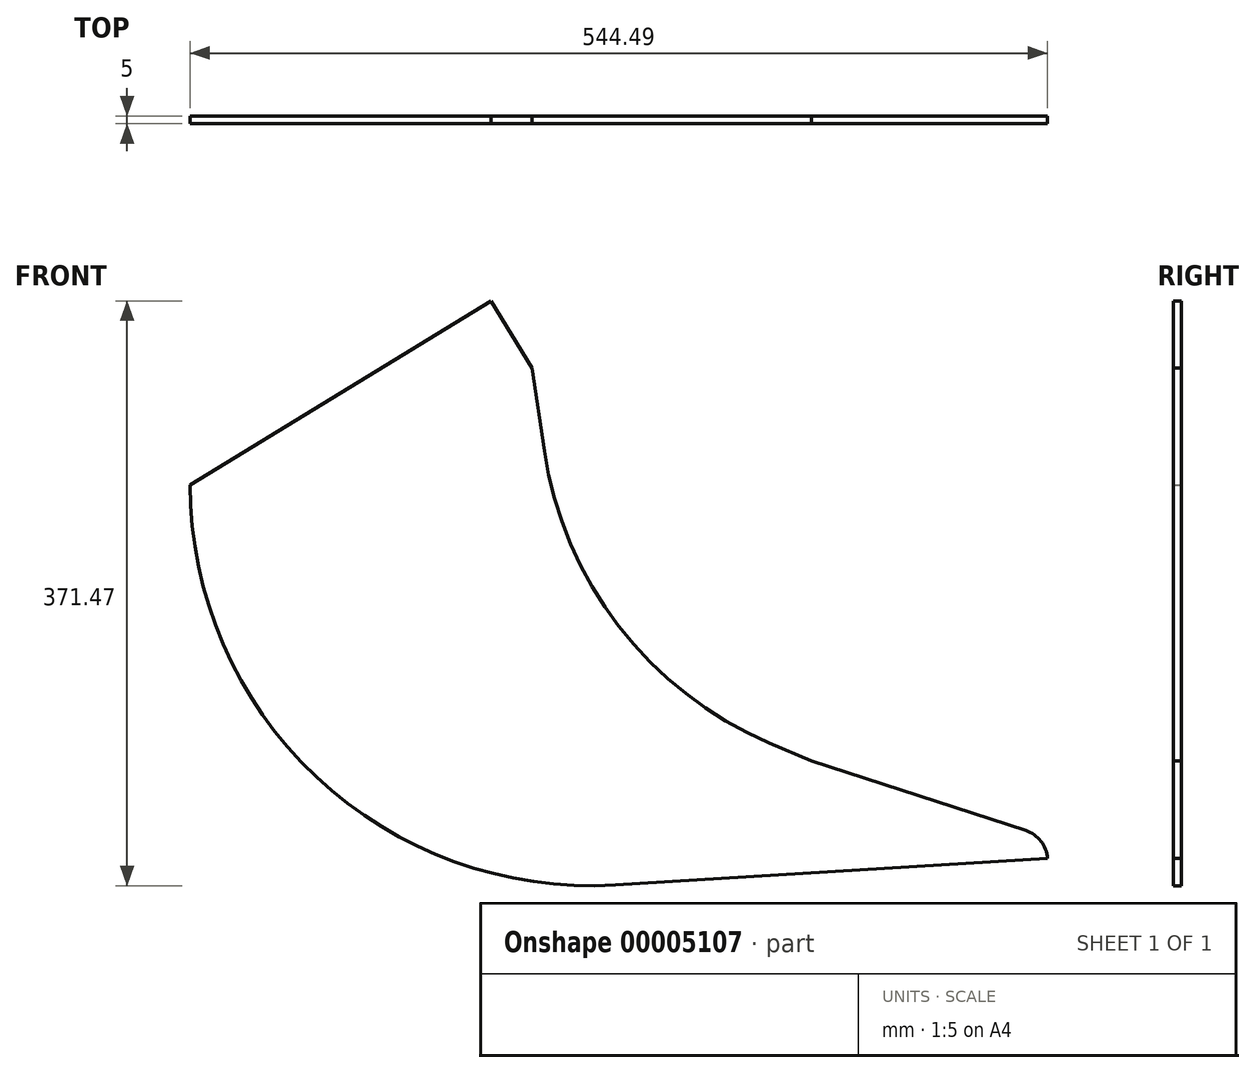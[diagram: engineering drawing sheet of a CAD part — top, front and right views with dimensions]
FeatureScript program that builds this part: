
annotation { "Feature Type Name" : "Feature", "Feature Type Description" : "" }
export const myFeature = defineFeature(function(context is Context, id is Id, definition is map)
    precondition{}
    {
        {
            var Q0;
            Q0=qCreatedBy(makeId("Front.planeOp"),FACE);
            var sketch = newSketch(context, id + "F0", { "sketchPlane" : qUnion([Q0])});
            skPoint(sketch, "E0.visualSharp", {"position": v(-263.52, -268.43) * mm});
            skArc(sketch, "E1", {"start": v(-326.76, 0) * mm, "mid": v(-246.64, -185.33) * mm, "end": v(-56.76, -253.99) * mm});
            skLineSegment(sketch, "E2", {"start": v(-56.76, -253.99) * mm, "end": v(217.73, -237.24) * mm});
            skLineSegment(sketch, "E3", {"start": v(217.73, -237.24) * mm, "end": v(217.73, -237.24) * mm});
            skLineSegment(sketch, "E4", {"start": v(-326.76, 0) * mm, "end": v(-135.75, 117.01) * mm});
            skLineSegment(sketch, "E5", {"start": v(-135.75, 117.01) * mm, "end": v(-109.64, 74.38) * mm});
            skLineSegment(sketch, "E6", {"start": v(-110.08, 75.56) * mm, "end": v(-109.64, 74.38) * mm});
            skLineSegment(sketch, "E7", {"start": v(67.92, -175.3) * mm, "end": v(203.94, -219.44) * mm});
            skPoint(sketch, "E8.visualSharp", {"position": v(216.9, -223.64) * mm});
            skArc(sketch, "E8.filletArc", {"start": v(217.73, -237.24) * mm, "mid": v(213.58, -226.21) * mm, "end": v(203.94, -219.44) * mm});
            skLineSegment(sketch, "E9", {"start": v(-109.64, 74.38) * mm, "end": v(-101.84, 21.7) * mm});
            skLineSegment(sketch, "E10", {"start": v(40.95, -163.72) * mm, "end": v(67.92, -175.3) * mm});
            skPoint(sketch, "E11.visualSharp", {"position": v(-82.22, -110.88) * mm});
            skArc(sketch, "E11.filletArc", {"start": v(-101.84, 21.7) * mm, "mid": v(-54.58, -89.6) * mm, "end": v(40.95, -163.72) * mm});
            skSolve(sketch);
        }
        {
            var Q0;
            Q0=makeQuery(id+"F0.imprint","IMPRINT",FACE,{"disambiguationData":[TD([[makeQuery(id+"F0.imprint","IMPRINT",EDGE,{"derivedFrom":sQuery(id+"F0.wireOp",EDGE,"E1")}),1.0]])]});
            extrude(context, id + "F1", {"entities" : qUnion([Q0]), "depth" : 5 * mm});
        }
    });
